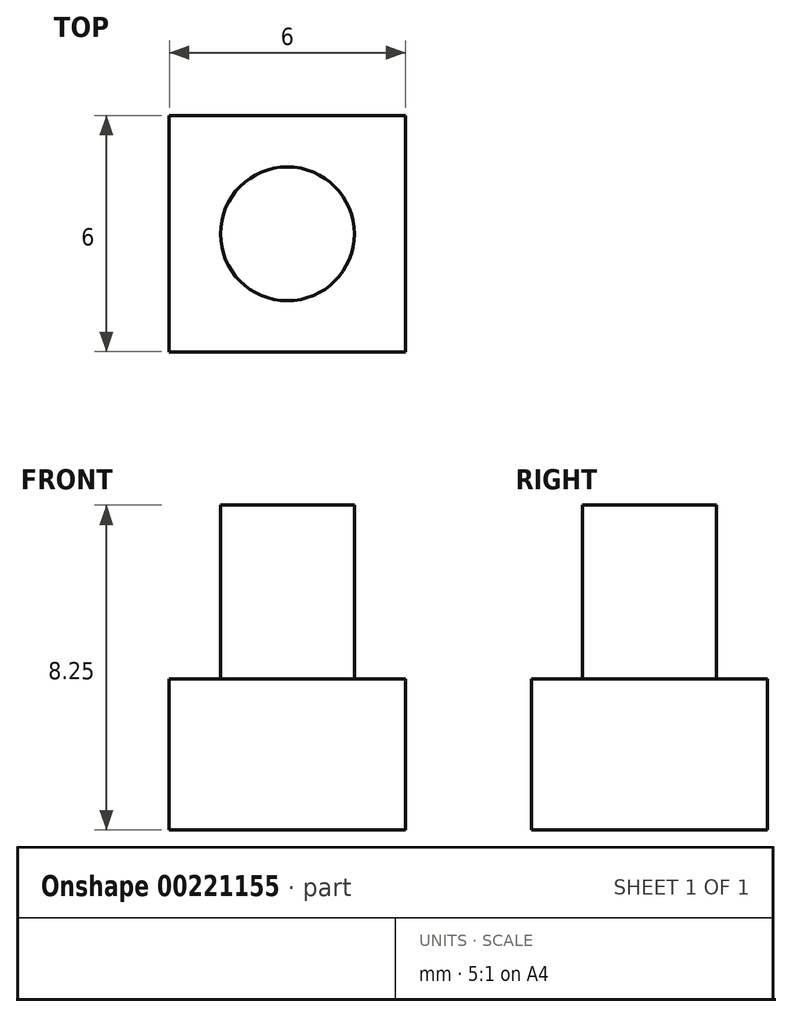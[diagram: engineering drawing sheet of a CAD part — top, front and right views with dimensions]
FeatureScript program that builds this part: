
annotation { "Feature Type Name" : "Feature", "Feature Type Description" : "" }
export const myFeature = defineFeature(function(context is Context, id is Id, definition is map)
    precondition{}
    {
        {
            var Q0;
            Q0=qCreatedBy(makeId("Top.planeOp"),FACE);
            var sketch = newSketch(context, id + "F0", { "sketchPlane" : qUnion([Q0])});
            skLineSegment(sketch, "E0.bottom", {"start": v(-19.37, 2.66) * mm, "end": v(-13.37, 2.66) * mm});
            skLineSegment(sketch, "E0.top", {"start": v(-19.37, -3.34) * mm, "end": v(-13.37, -3.34) * mm});
            skLineSegment(sketch, "E0.left", {"start": v(-19.37, 2.66) * mm, "end": v(-19.37, -3.34) * mm});
            skLineSegment(sketch, "E0.right", {"start": v(-13.37, 2.66) * mm, "end": v(-13.37, -3.34) * mm});
            skCircle(sketch, "E1", {"center": v(-16.37, -0.34) * mm, "radius": 1.7 * mm});
            skPoint(sketch, "E2", {"position": v(-16.37, -3.34) * mm});
            skPoint(sketch, "E3", {"position": v(-19.37, -0.34) * mm});
            skSolve(sketch);
        }
        {
            var Q0;
            Q0=makeQuery(id+"F0.imprint","IMPRINT",FACE,{"disambiguationData":[TD([[makeQuery(id+"F0.imprint","IMPRINT",EDGE,{"derivedFrom":sQuery(id+"F0.wireOp",EDGE,"E0.bottom")}),-1.0]])]});
            var Q1;
            Q1=makeQuery(id+"F0.imprint","IMPRINT",FACE,{"disambiguationData":[TD([[makeQuery(id+"F0.imprint","IMPRINT",EDGE,{"derivedFrom":sQuery(id+"F0.wireOp",EDGE,"E1")}),1.0]])]});
            extrude(context, id + "F1", {"entities" : qUnion([Q0, Q1]), "depth" : (5.34 - 1.5) * mm});
        }
        {
            var Q0;
            Q0=makeQuery(id+"F0.imprint","IMPRINT",FACE,{"disambiguationData":[TD([[makeQuery(id+"F0.imprint","IMPRINT",EDGE,{"derivedFrom":sQuery(id+"F0.wireOp",EDGE,"E1")}),1.0]])]});
            extrude(context, id + "F2", {"entities" : qUnion([Q0]), "operationType" : NewBodyOperationType.ADD, "depth" : (9.75 - 1.5) * mm});
        }
    });
